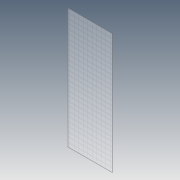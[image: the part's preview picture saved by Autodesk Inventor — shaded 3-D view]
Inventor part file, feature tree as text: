
AUTODESK INVENTOR PART (.ipt)
format: ipt  version: 2012 (Build 160160000, 160)  size: 76,288 bytes
history: native  units: in
note: dims shown in document units (in); Inventor stores cm internally (conversion verified against a paired STEP export)
features: extrude x1, sketch x1
ambient origin geometry x8: Origin, YZ Plane, XZ Plane, XY Plane, X Axis, Y Axis, Z Axis, Center Point
bodies: Solid1 (feature_tree)
feature tree (2):
  extrude  "Extrusion1"  Depth=24.0in
  sketch  "Sketch1"  dims[d0=65.0in d1=24.0in d2=0.125in d3=0.0in]
